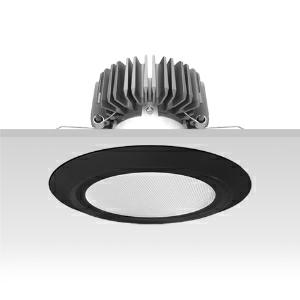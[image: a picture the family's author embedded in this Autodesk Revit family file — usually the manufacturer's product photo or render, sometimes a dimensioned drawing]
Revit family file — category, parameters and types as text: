
# Revit family: 3f_filippi_-_3f_reno_bianco_ampio_3f_filippi_-_30621_a01049_-_3f_reno_200_wh_2000-840_wide___smp_bk_e793
name_source: partatom
category: Lighting Fixtures
units: mm (PartAtom-declared; Revit-internal decimal feet)

## family parameters
Cut with Voids When Loaded = No
Host = Face
Light Source = No
Part Type = Normal
Room Calculation Point = No
Round Connector Dimension = Use Diameter
Shared = No

## types (1)
- 3F Filippi - 3F Reno Bianco Ampio (1 x LED, 1723 lm, 20 W, 4000 K)
    Apparent Load = 20 VA
    Approval mark = CE
    CIE Flux Codes = 74 92 98 100 100
    Color Rendering = 80
    Color Temperature = 4000 K
    Control Gear = Electronic ballast
    Default Elevation = 1800 mm
    Description = ILLUMINOTECHNICAL
Luminous efficiency 100% (DLOR 100%, ULOR 0%).
Initial luminous flux of the luminaire 1723 lm.
Direct symmetric wide distribution.
Installation Interdistance Transv.D = 1.06 x hu - Long.D = 1.04 x hu.
Average luminance <3000 cd/m² for radial angles >65°.
Tabular UGR (CIE 117 - 4H-8H; S=0.25H; 70/50/20): RUG 21.4 - 21.3.
Beam angle: 70° - 69°.
Luminous efficacy 86 lm/W.
Lifetime (L90/B10): 30000 h. (tq+25°C)
Lifetime (L85/B10): 50000 h. (tq+25°C)
Lifetime (L70/B10): 80000 h. (tq+25°C)
Sudden decreased luminous flux after 50000 hours: 0% (C0).
Photobiological safety in compliance with IEC/TR 62778: RG0 risk exempt, (IEC 62471).
In compliance with IEC/EN 62722-2-1 - IEC/EN 62717 standards.

SOURCE
Compact LED module 2000/840.
Energy efficiency class (UE 2019/2020 - UE 2019/2015): D.
CIE 13.3 Colour rendering index: CRI >80 (R9 <50%).
IES TM-30 Fidelity Index: Rf = 84 Rg = 95.
CCT nominal colour temperature 4000 K.
Colour initial tolerance (MacAdam): SDCM 3.
Zhaga Book 3 compliant.

MECHANICAL
Passive heat dissipator in die-casting aluminium, oversized, for optimum thermal management of the LED module.
Parabolic element with graduated/concentric rings in white polycarbonate.
Transparent external lens with glossy and satin differentiated surfaces, with a cooling and anti-insect system in methacrylate (PMMA).
Fastening spring clips in stainless steel.
Dimensions: diameter 226 mm, height 146 mm. Weight 1 kg.
IP44 protection degree for exposed part, IP20 for recessed part.
Mechanical strength to impacts IK05 (0.7 joule).
Glow-wire test resistance 650°C.

ELECTRICAL
Wiring on a separate unit.
Halogen Free electronic wiring 230V-50/60Hz, power factor 0.95, THD <25%, constant output current, SELV, class II, 1 driver.
Power of the luminaire 20 W.
ENEC - CE.
SAFE FLICKER: PstLM=<1 and SVM=<0.4 (IEC TR 61547-1 and IEC TR 63158), to ensure a more comfortable and safe light.
Luminaire compliant with EN 60598-2-22 for power supply from a centralised emergency system CPSS (Central Power Supply System), not incorporated in the luminaire - high risk areas excluded. The default power and flux are 100% in AC and 100% in DC.
Ambient temperature from 0°C to +25°C.
Temperature class T6 max 85°C.
Relative humidity UR: <85%.

INSTALLATION
Pull-up recessed fitting.
False ceiling carving: 200 mm.
All accessories dedicated to this product are available on the Catalog and on our website www.3F-Filippi.com.

ACCESSORIES
A01049 - Anti-glare microprismatic SMP diffuser in methacrylate (PMMA), locked and in line with the trim, in black polycarbonate.

APPLICATIONS
Suitable product for food production plants (HACCP), IFS (Food Version 6), BRC (GSFS Food Version 7).
Environments: architectural, commercial, exhibition areas, transit areas, corridors, shops, display windows, service areas.
In false ceilings with narrow voids.

WARNING
Luminaire designed for disposal/recycling at end-of-life.
Replaceable (LED only) light source by a professional. Replaceable control gear by a professional.
    Height = 0 mm  [stored 0 ft]
    Lamp = 1 x LED
    Lamp Light Flux = 1723 lm
    Lamp Power = 20 W
    Lamp count = 1
    Length = 226 mm
    Lifetime = 50000 h
    Luminous efficacy = 86 lm/W
    Manufacturer = 3F Filippi
    ModVariant = No
    Model = 3F Filippi - 30621+A01049 - 3F Reno 200 WH 2000-840 WIDE + SMP BK
    Mounting Place = Ceiling
    Mounting Type = Recessed
    Number of Poles = 1
    OnlyDefault = Yes
    Power Factor = 1
    Product Name = 3F Filippi - 3F Reno Bianco Ampio
    Product group = recessed luminaire
    ProductGroupID = 4
    Protection Class = Protection class II
    Protection Degree = IP 20
    RLX_Detail_Level = 1
    RLX_Emergency_Light_Flux = 0 lm
    RLX_Emergency_Type = 0
    RLX_Emergency_Type_DB = No
    RlxData = <blob elided: 98281 chars, md5=85f1de35>
    Socket = socket
    Standby Power = 0 W
    System Light Flux = 1723 lm
    System Power = 20 W
    Type Comments = Product without accessories
    Type Image = 3ffilippi_3f_reno_200_bk_vs_smp.jpg
    URL = http://relux.com
    VarID = ---
    Voltage = 0 V
    Weight = 0.00 kg
    Width = 0 mm  [stored 0 ft]

note: [stored X ft] marks values corroborated as IEEE doubles in the binary element streams (Revit-internal decimal feet)

## geometry (parser evidence)
native form markers: Blend x4, Sweep x10
no freeform markers — native parametric forms only
